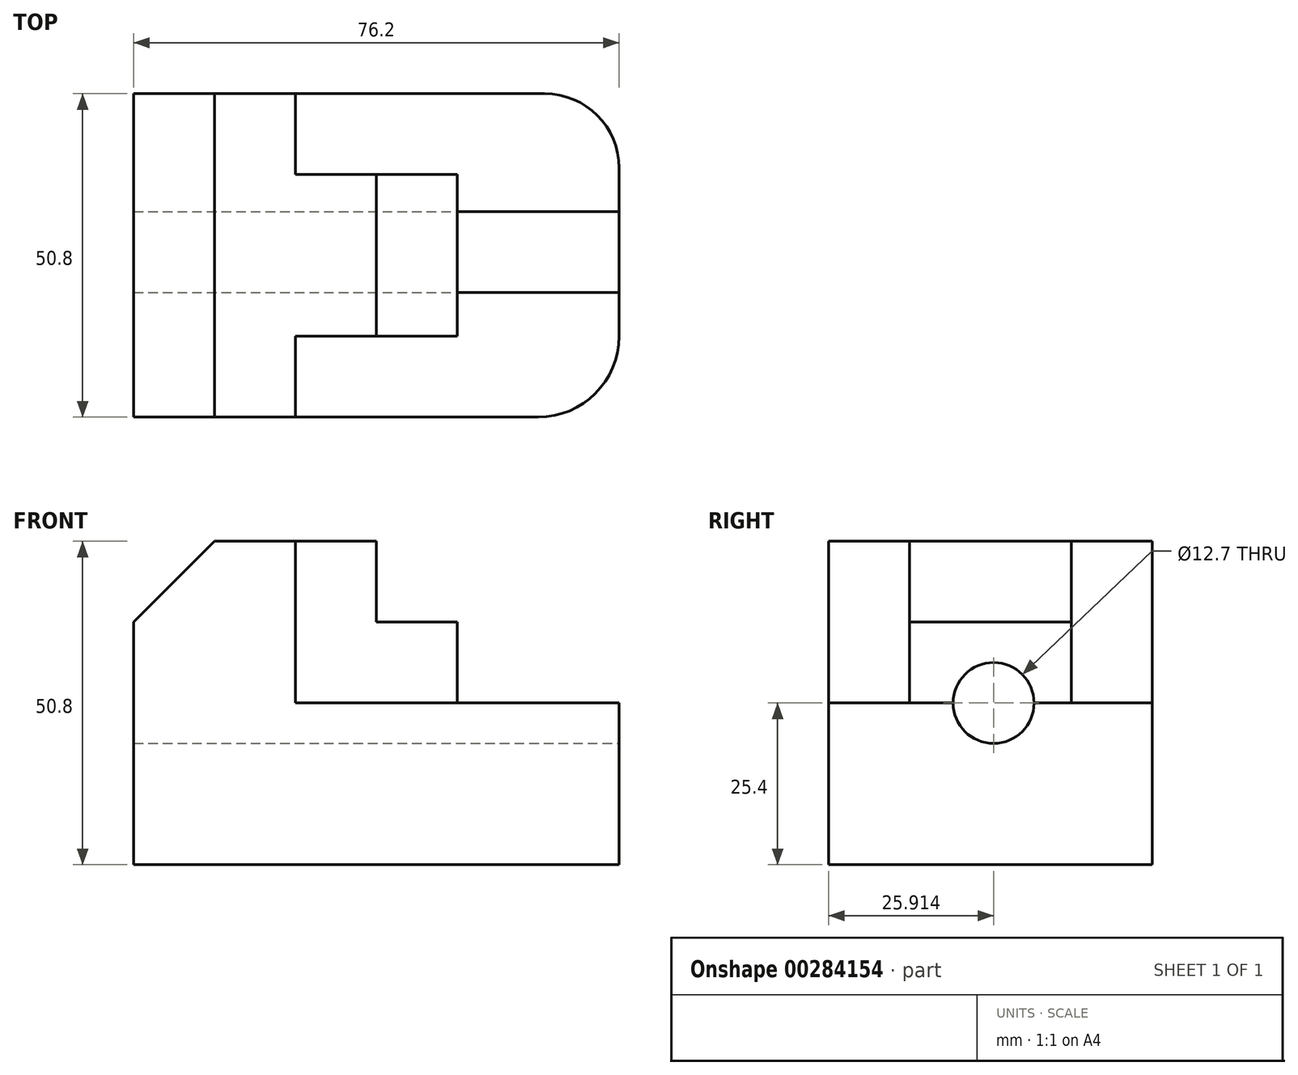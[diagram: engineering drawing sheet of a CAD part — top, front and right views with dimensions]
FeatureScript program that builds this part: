
annotation { "Feature Type Name" : "Feature", "Feature Type Description" : "" }
export const myFeature = defineFeature(function(context is Context, id is Id, definition is map)
    precondition{}
    {
        {
            var Q0;
            Q0=qCreatedBy(makeId("Top.planeOp"),FACE);
            var sketch = newSketch(context, id + "F0", { "sketchPlane" : qUnion([Q0])});
            skLineSegment(sketch, "E0.bottom", {"start": v(0, 0) * mm, "end": v(76.2, 0) * mm});
            skLineSegment(sketch, "E0.top", {"start": v(0, 50.8) * mm, "end": v(76.2, 50.8) * mm});
            skLineSegment(sketch, "E0.left", {"start": v(0, 0) * mm, "end": v(0, 50.8) * mm});
            skLineSegment(sketch, "E0.right", {"start": v(76.2, 0) * mm, "end": v(76.2, 50.8) * mm});
            skArc(sketch, "E1", {"start": v(64.53, 50.8) * mm, "mid": v(72.78, 47.38) * mm, "end": v(76.2, 39.13) * mm});
            skSolve(sketch);
        }
        {
            var Q0;
            Q0=makeQuery(id+"F0.imprint","IMPRINT",FACE,{"disambiguationData":[TD([[makeQuery(id+"F0.imprint","IMPRINT",EDGE,{"derivedFrom":sQuery(id+"F0.wireOp",EDGE,"E0.bottom")}),1.0]])]});
            extrude(context, id + "F1", {"entities" : qUnion([Q0]), "endBound" : BoundingType.SYMMETRIC, "depth" : 50.8 * mm});
        }
        {
            var Q0;
            Q0=makeQuery(id+"F1.opExtrude","SWEPT_FACE",FACE,{"disambiguationData":[OSD([sQuery(id+"F0.wireOp",EDGE,"E0.bottom")])]});
            var sketch = newSketch(context, id + "F2", { "sketchPlane" : qUnion([Q0])});
            skLineSegment(sketch, "E2", {"start": v(0, 25.4) * mm, "end": v(12.7, 25.4) * mm});
            skLineSegment(sketch, "E3", {"start": v(12.7, 25.4) * mm, "end": v(0, 12.7) * mm});
            skLineSegment(sketch, "E4", {"start": v(0, 12.7) * mm, "end": v(0, 25.4) * mm});
            skSolve(sketch);
        }
        {
            var Q0;
            Q0=makeQuery(id+"F2.imprint","IMPRINT",FACE,{"disambiguationData":[TD([[makeQuery(id+"F2.imprint","IMPRINT",EDGE,{"derivedFrom":sQuery(id+"F2.wireOp",EDGE,"E2")}),-1.0]])]});
            extrude(context, id + "F3", {"entities" : qUnion([Q0]), "operationType" : NewBodyOperationType.REMOVE, "endBound" : BoundingType.THROUGH_ALL, "oppositeDirection" : true, "depth" : 25.4 * mm});
        }
        {
            var Q0;
            Q0=makeQuery(id+"F1.opExtrude","CAP_FACE",FACE,{"disambiguationData":[OSD([sQuery(id+"F0.wireOp",EDGE,"E0.bottom"),sQuery(id+"F0.wireOp",EDGE,"E0.top"),sQuery(id+"F0.wireOp",EDGE,"E0.left"),sQuery(id+"F0.wireOp",EDGE,"E0.right")])],"isStart":false});
            var sketch = newSketch(context, id + "F4", { "sketchPlane" : qUnion([Q0])});
            skLineSegment(sketch, "E5.bottom", {"start": v(25.4, 50.8) * mm, "end": v(50.8, 50.8) * mm});
            skLineSegment(sketch, "E5.top", {"start": v(25.4, 38.1) * mm, "end": v(50.8, 38.1) * mm});
            skLineSegment(sketch, "E5.left", {"start": v(25.4, 50.8) * mm, "end": v(25.4, 38.1) * mm});
            skLineSegment(sketch, "E5.right", {"start": v(50.8, 50.8) * mm, "end": v(50.8, 38.1) * mm});
            skLineSegment(sketch, "E6.bottom", {"start": v(25.4, 0) * mm, "end": v(50.8, 0) * mm});
            skLineSegment(sketch, "E6.top", {"start": v(25.4, 12.7) * mm, "end": v(50.8, 12.7) * mm});
            skLineSegment(sketch, "E6.left", {"start": v(25.4, 0) * mm, "end": v(25.4, 12.7) * mm});
            skLineSegment(sketch, "E6.right", {"start": v(50.8, 0) * mm, "end": v(50.8, 12.7) * mm});
            skArc(sketch, "E7", {"start": v(63.5, 0) * mm, "mid": v(72.48, 3.72) * mm, "end": v(76.2, 12.7) * mm});
            skSolve(sketch);
        }
        {
            var Q0;
            Q0=makeQuery(id+"F4.imprint","IMPRINT",FACE,{"disambiguationData":[TD([[makeQuery(id+"F4.imprint","IMPRINT",EDGE,{"derivedFrom":sQuery(id+"F4.wireOp",EDGE,"E5.bottom")}),-1.0]])]});
            var Q1;
            Q1=makeQuery(id+"F4.imprint","IMPRINT",FACE,{"disambiguationData":[TD([[makeQuery(id+"F4.imprint","IMPRINT",EDGE,{"derivedFrom":sQuery(id+"F4.wireOp",EDGE,"E6.bottom")}),1.0]])]});
            extrude(context, id + "F5", {"entities" : qUnion([Q0, Q1]), "operationType" : NewBodyOperationType.REMOVE, "oppositeDirection" : true, "depth" : 25.4 * mm});
        }
        {
            var Q0;
            Q0=makeQuery(id+"F4.imprint","IMPRINT",FACE,{"disambiguationData":[TD([[makeQuery(id+"F4.imprint","IMPRINT",EDGE,{"derivedFrom":sQuery(id+"F4.wireOp",EDGE,"E5.top")}),-1.0]])]});
            var sketch = newSketch(context, id + "F6", { "sketchPlane" : qUnion([Q0])});
            skLineSegment(sketch, "E8.bottom", {"start": v(76.2, 50.8) * mm, "end": v(50.8, 50.8) * mm});
            skLineSegment(sketch, "E8.top", {"start": v(76.2, 0) * mm, "end": v(50.8, 0) * mm});
            skLineSegment(sketch, "E8.left", {"start": v(76.2, 50.8) * mm, "end": v(76.2, 0) * mm});
            skLineSegment(sketch, "E8.right", {"start": v(50.8, 50.8) * mm, "end": v(50.8, 0) * mm});
            skSolve(sketch);
        }
        {
            var Q0;
            Q0 = qSketchRegion(id + "F6", true);
            var Q1;
            Q1=makeQuery(id+"F5.boolean.opBoolean","COPY",FACE,{"derivedFrom":makeQuery(id+"F5.opExtrude","CAP_FACE",FACE,{"disambiguationData":[OSD([sQuery(id+"F4.wireOp",EDGE,"E6.bottom"),sQuery(id+"F4.wireOp",EDGE,"E6.top"),sQuery(id+"F4.wireOp",EDGE,"E6.left"),sQuery(id+"F4.wireOp",EDGE,"E6.right")])],"isStart":false})});
            extrude(context, id + "F7", {"entities" : qUnion([Q0]), "operationType" : NewBodyOperationType.REMOVE, "endBound" : BoundingType.UP_TO_SURFACE, "oppositeDirection" : true, "endBoundEntityFace" : qUnion([Q1]), "depth" : 25.4 * mm});
        }
        {
            var Q0;
            Q0=makeQuery(id+"F4.imprint","IMPRINT",FACE,{"disambiguationData":[TD([[makeQuery(id+"F4.imprint","IMPRINT",EDGE,{"derivedFrom":sQuery(id+"F4.wireOp",EDGE,"E5.top")}),-1.0]])]});
            var sketch = newSketch(context, id + "F8", { "sketchPlane" : qUnion([Q0])});
            skLineSegment(sketch, "E9.bottom", {"start": v(38.1, 38.1) * mm, "end": v(50.8, 38.1) * mm});
            skLineSegment(sketch, "E9.top", {"start": v(38.1, 12.7) * mm, "end": v(50.8, 12.7) * mm});
            skLineSegment(sketch, "E9.left", {"start": v(38.1, 38.1) * mm, "end": v(38.1, 12.7) * mm});
            skLineSegment(sketch, "E9.right", {"start": v(50.8, 38.1) * mm, "end": v(50.8, 12.7) * mm});
            skSolve(sketch);
        }
        {
            var Q0;
            Q0 = qSketchRegion(id + "F8", true);
            extrude(context, id + "F9", {"entities" : qUnion([Q0]), "operationType" : NewBodyOperationType.REMOVE, "oppositeDirection" : true, "depth" : 12.7 * mm});
        }
        {
            var Q0;
            {var subQ0=sQuery(id+"F4.wireOp",EDGE,"E7");Q0=makeQuery(id+"F4.imprint","IMPRINT",FACE,{"disambiguationData":[TD([[makeQuery(id+"F4.imprint","IMPRINT",EDGE,{"derivedFrom":subQ0}),-1.0]])]});}
            extrude(context, id + "F10", {"entities" : qUnion([Q0]), "operationType" : NewBodyOperationType.REMOVE, "endBound" : BoundingType.THROUGH_ALL, "oppositeDirection" : true, "depth" : 25.4 * mm});
        }
        {
            var Q0;
            Q0=makeQuery(id+"F1.opExtrude","SWEPT_FACE",FACE,{"disambiguationData":[OSD([sQuery(id+"F0.wireOp",EDGE,"E0.right")])]});
            var sketch = newSketch(context, id + "F11", { "sketchPlane" : qUnion([Q0])});
            skCircle(sketch, "E10", {"center": v(25.91, 0) * mm, "radius": 6.35 * mm});
            skSolve(sketch);
        }
        {
            var Q0;
            {var subQ0=sQuery(id+"F11.wireOp",EDGE,"E10");var subQ1=sQuery(id+"F6.wireOp",EDGE,"E8.left");var subQ2=makeQuery(id+"F6.imprint","INTERSECT",VERTEX,{"derivedFrom":[makeQuery(id+"F4.imprint","IMPRINT",EDGE,{"derivedFrom":sQuery(id+"F4.wireOp",EDGE,"E7")}),subQ1]});var subQ3=makeQuery(id+"F6.imprint","INTERSECT",VERTEX,{"derivedFrom":[makeQuery(id+"F4.imprint","IMPRINT",EDGE,{"derivedFrom":makeQuery(id+"F1.opExtrude","CAP_EDGE",EDGE,{"disambiguationData":[OSD([sQuery(id+"F0.wireOp",EDGE,"E1")])],"isStart":false})}),subQ1]});var subQ4=makeQuery(id+"F7.boolean.opBoolean","COPY",EDGE,{"derivedFrom":makeQuery(id+"F7.opExtrude","TWEAK_EDGE",EDGE,{"derivedFrom":[makeQuery(id+"F5.boolean.opBoolean","COPY",FACE,{"derivedFrom":makeQuery(id+"F5.opExtrude","CAP_FACE",FACE,{"disambiguationData":[OSD([sQuery(id+"F4.wireOp",EDGE,"E6.bottom"),sQuery(id+"F4.wireOp",EDGE,"E6.top"),sQuery(id+"F4.wireOp",EDGE,"E6.left"),sQuery(id+"F4.wireOp",EDGE,"E6.right")])],"isStart":false})}),makeQuery(id+"F6.imprint","IMPRINT",EDGE,{"disambiguationData":[TD([[subQ3,1.0],[makeQuery(id+"F6.imprint","INTERSECT",VERTEX,{"derivedFrom":[sQuery(id+"F6.wireOp",EDGE,"E8.bottom"),subQ1]}),-1.0]])],"derivedFrom":subQ1}),makeQuery(id+"F6.imprint","IMPRINT",EDGE,{"disambiguationData":[TD([[subQ3,1.0],[subQ2,-1.0]])],"derivedFrom":subQ1}),makeQuery(id+"F6.imprint","IMPRINT",EDGE,{"disambiguationData":[TD([[subQ2,-1.0],[makeQuery(id+"F6.imprint","INTERSECT",VERTEX,{"derivedFrom":[sQuery(id+"F6.wireOp",EDGE,"E8.top"),subQ1]}),1.0]])],"derivedFrom":subQ1})]})});var subQ5=makeQuery(id+"F11.imprint","INTERSECT",VERTEX,{"disambiguationData":[OD(0.0)],"derivedFrom":[subQ4,subQ0]});Q0=makeQuery(id+"F11.imprint","IMPRINT",FACE,{"disambiguationData":[TD([[makeQuery(id+"F11.imprint","IMPRINT",EDGE,{"disambiguationData":[TD([[subQ5,1.0]])],"derivedFrom":subQ0}),1.0]])]});}
            var Q1;
            {var subQ0=sQuery(id+"F11.wireOp",EDGE,"E10");var subQ1=sQuery(id+"F6.wireOp",EDGE,"E8.left");var subQ2=makeQuery(id+"F6.imprint","INTERSECT",VERTEX,{"derivedFrom":[makeQuery(id+"F4.imprint","IMPRINT",EDGE,{"derivedFrom":sQuery(id+"F4.wireOp",EDGE,"E7")}),subQ1]});var subQ3=makeQuery(id+"F6.imprint","INTERSECT",VERTEX,{"derivedFrom":[makeQuery(id+"F4.imprint","IMPRINT",EDGE,{"derivedFrom":makeQuery(id+"F1.opExtrude","CAP_EDGE",EDGE,{"disambiguationData":[OSD([sQuery(id+"F0.wireOp",EDGE,"E1")])],"isStart":false})}),subQ1]});var subQ4=makeQuery(id+"F7.boolean.opBoolean","COPY",EDGE,{"derivedFrom":makeQuery(id+"F7.opExtrude","TWEAK_EDGE",EDGE,{"derivedFrom":[makeQuery(id+"F5.boolean.opBoolean","COPY",FACE,{"derivedFrom":makeQuery(id+"F5.opExtrude","CAP_FACE",FACE,{"disambiguationData":[OSD([sQuery(id+"F4.wireOp",EDGE,"E6.bottom"),sQuery(id+"F4.wireOp",EDGE,"E6.top"),sQuery(id+"F4.wireOp",EDGE,"E6.left"),sQuery(id+"F4.wireOp",EDGE,"E6.right")])],"isStart":false})}),makeQuery(id+"F6.imprint","IMPRINT",EDGE,{"disambiguationData":[TD([[subQ3,1.0],[makeQuery(id+"F6.imprint","INTERSECT",VERTEX,{"derivedFrom":[sQuery(id+"F6.wireOp",EDGE,"E8.bottom"),subQ1]}),-1.0]])],"derivedFrom":subQ1}),makeQuery(id+"F6.imprint","IMPRINT",EDGE,{"disambiguationData":[TD([[subQ3,1.0],[subQ2,-1.0]])],"derivedFrom":subQ1}),makeQuery(id+"F6.imprint","IMPRINT",EDGE,{"disambiguationData":[TD([[subQ2,-1.0],[makeQuery(id+"F6.imprint","INTERSECT",VERTEX,{"derivedFrom":[sQuery(id+"F6.wireOp",EDGE,"E8.top"),subQ1]}),1.0]])],"derivedFrom":subQ1})]})});var subQ5=makeQuery(id+"F11.imprint","INTERSECT",VERTEX,{"disambiguationData":[OD(0.0)],"derivedFrom":[subQ4,subQ0]});Q1=makeQuery(id+"F11.imprint","IMPRINT",FACE,{"disambiguationData":[TD([[makeQuery(id+"F11.imprint","IMPRINT",EDGE,{"disambiguationData":[TD([[subQ5,-1.0]])],"derivedFrom":subQ0}),1.0]])]});}
            extrude(context, id + "F12", {"entities" : qUnion([Q0, Q1]), "operationType" : NewBodyOperationType.REMOVE, "endBound" : BoundingType.THROUGH_ALL, "oppositeDirection" : true, "depth" : 25.4 * mm});
        }
    });
